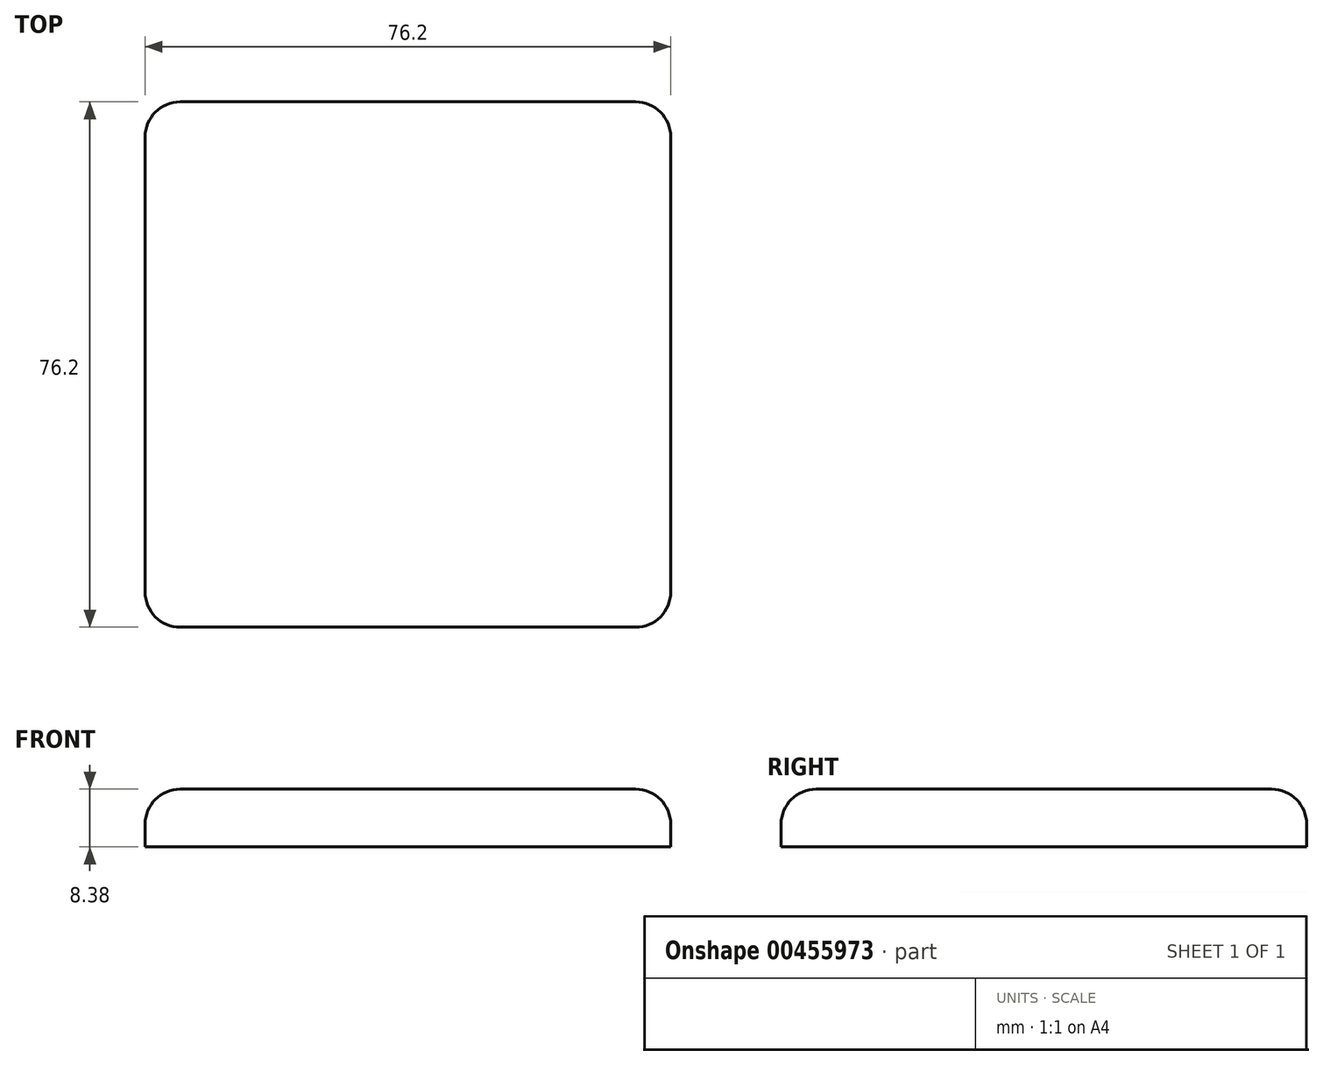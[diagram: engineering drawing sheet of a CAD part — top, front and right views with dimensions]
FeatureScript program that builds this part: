
annotation { "Feature Type Name" : "Feature", "Feature Type Description" : "" }
export const myFeature = defineFeature(function(context is Context, id is Id, definition is map)
    precondition{}
    {
        {
            var Q0;
            Q0=qCreatedBy(makeId("Top.planeOp"),FACE);
            var sketch = newSketch(context, id + "F0", { "sketchPlane" : qUnion([Q0])});
            skLineSegment(sketch, "E0.bottom", {"start": v(38.1, -38.1) * mm, "end": v(-38.1, -38.1) * mm});
            skLineSegment(sketch, "E0.top", {"start": v(38.1, 38.1) * mm, "end": v(-38.1, 38.1) * mm});
            skLineSegment(sketch, "E0.left", {"start": v(38.1, -38.1) * mm, "end": v(38.1, 38.1) * mm});
            skLineSegment(sketch, "E0.right", {"start": v(-38.1, -38.1) * mm, "end": v(-38.1, 38.1) * mm});
            skPoint(sketch, "E0.middle", {"position": v(0, 0) * mm});
            skSolve(sketch);
        }
        {
            var Q0;
            Q0 = qSketchRegion(id + "F0", true);
            extrude(context, id + "F1", {"entities" : qUnion([Q0]), "depth" : 8.38 * mm});
        }
        {
            var Q0;
            Q0=makeQuery(id+"F1.opExtrude","SWEPT_EDGE",EDGE,{"disambiguationData":[OSD([sQuery(id+"F0.wireOp",EDGE,"E0.bottom"),sQuery(id+"F0.wireOp",EDGE,"E0.right")])]});
            var Q1;
            Q1=makeQuery(id+"F1.opExtrude","SWEPT_EDGE",EDGE,{"disambiguationData":[OSD([sQuery(id+"F0.wireOp",EDGE,"E0.bottom"),sQuery(id+"F0.wireOp",EDGE,"E0.left")])]});
            var Q2;
            Q2=makeQuery(id+"F1.opExtrude","SWEPT_EDGE",EDGE,{"disambiguationData":[OSD([sQuery(id+"F0.wireOp",EDGE,"E0.top"),sQuery(id+"F0.wireOp",EDGE,"E0.left")])]});
            var Q3;
            Q3=makeQuery(id+"F1.opExtrude","SWEPT_EDGE",EDGE,{"disambiguationData":[OSD([sQuery(id+"F0.wireOp",EDGE,"E0.top"),sQuery(id+"F0.wireOp",EDGE,"E0.right")])]});
            var Q4;
            Q4=makeQuery(id+"F1.opExtrude","CAP_EDGE",EDGE,{"disambiguationData":[OSD([sQuery(id+"F0.wireOp",EDGE,"E0.left")])],"isStart":false});
            var Q5;
            Q5=makeQuery(id+"F1.opExtrude","CAP_EDGE",EDGE,{"disambiguationData":[OSD([sQuery(id+"F0.wireOp",EDGE,"E0.top")])],"isStart":false});
            var Q6;
            Q6=makeQuery(id+"F1.opExtrude","CAP_EDGE",EDGE,{"disambiguationData":[OSD([sQuery(id+"F0.wireOp",EDGE,"E0.right")])],"isStart":false});
            var Q7;
            Q7=makeQuery(id+"F1.opExtrude","CAP_EDGE",EDGE,{"disambiguationData":[OSD([sQuery(id+"F0.wireOp",EDGE,"E0.bottom")])],"isStart":false});
            fillet(context, id + "F2", {"entities" : qUnion([Q0, Q1, Q2, Q3, Q4, Q5, Q6, Q7]), "radius" : 5.08 * mm, "tangentPropagation" : true, "allowEdgeOverflow" : false});
        }
    });
